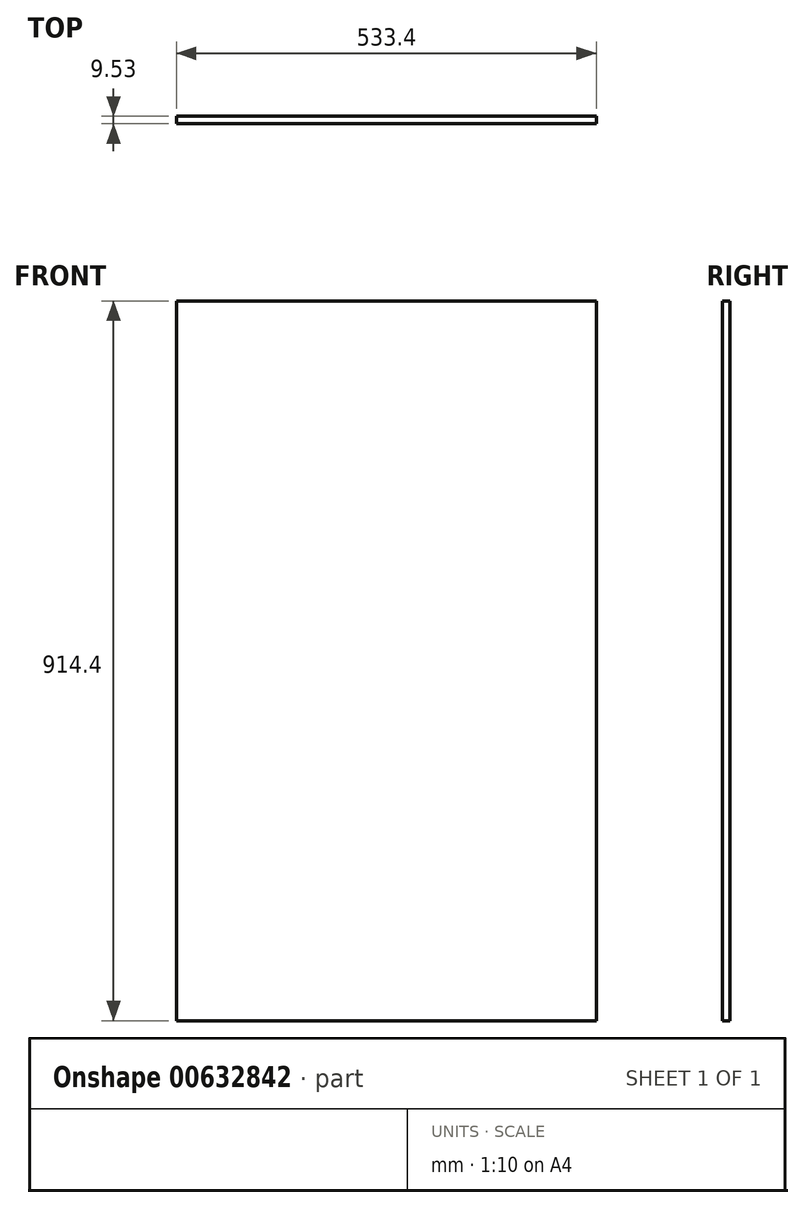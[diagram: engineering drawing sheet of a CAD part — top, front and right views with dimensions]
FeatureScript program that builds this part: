
annotation { "Feature Type Name" : "Feature", "Feature Type Description" : "" }
export const myFeature = defineFeature(function(context is Context, id is Id, definition is map)
    precondition{}
    {
        {
            var Q0;
            Q0=qCreatedBy(makeId("Front.planeOp"),FACE);
            var sketch = newSketch(context, id + "F0", { "sketchPlane" : qUnion([Q0])});
            skLineSegment(sketch, "E0.bottom", {"start": v(266.7, 457.2) * mm, "end": v(-266.7, 457.2) * mm});
            skLineSegment(sketch, "E0.top", {"start": v(266.7, -457.2) * mm, "end": v(-266.7, -457.2) * mm});
            skLineSegment(sketch, "E0.left", {"start": v(266.7, 457.2) * mm, "end": v(266.7, -457.2) * mm});
            skLineSegment(sketch, "E0.right", {"start": v(-266.7, 457.2) * mm, "end": v(-266.7, -457.2) * mm});
            skPoint(sketch, "E0.middle", {"position": v(0, 0) * mm});
            skSolve(sketch);
        }
        {
            var Q0;
            Q0=makeQuery(id+"F0.imprint","IMPRINT",FACE,{"disambiguationData":[TD([[makeQuery(id+"F0.imprint","IMPRINT",EDGE,{"derivedFrom":sQuery(id+"F0.wireOp",EDGE,"E0.bottom")}),1.0]])]});
            extrude(context, id + "F1", {"entities" : qUnion([Q0]), "depth" : 9.52 * mm, "offsetDistance" : 25.4 * mm});
        }
    });
